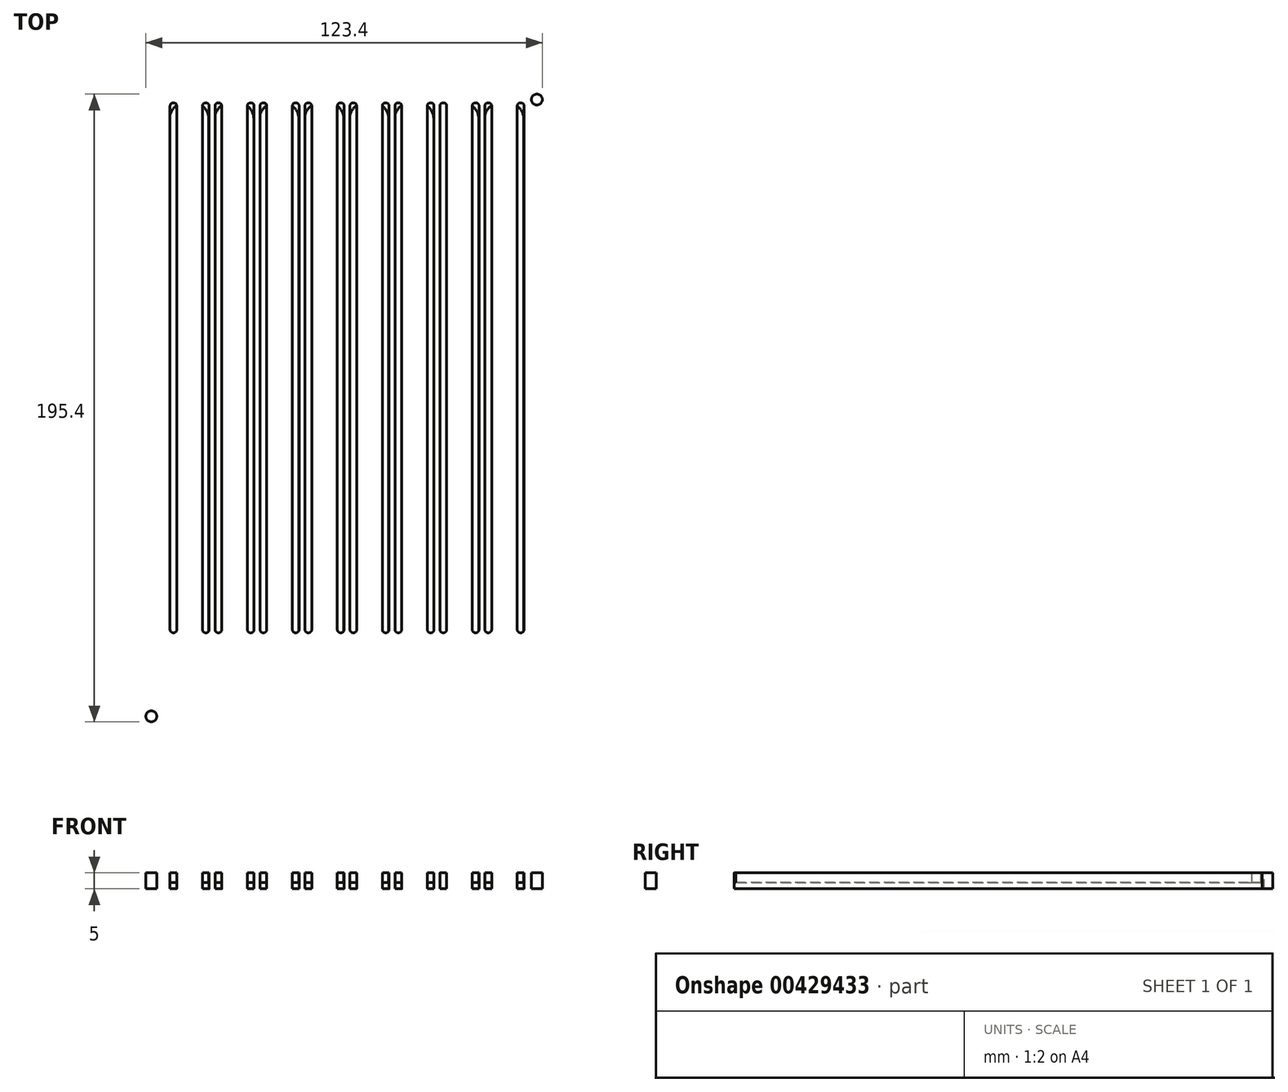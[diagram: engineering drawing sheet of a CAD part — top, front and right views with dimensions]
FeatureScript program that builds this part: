
annotation { "Feature Type Name" : "Feature", "Feature Type Description" : "" }
export const myFeature = defineFeature(function(context is Context, id is Id, definition is map)
    precondition{}
    {
        {
            var Q0;
            Q0=qCreatedBy(makeId("Top.planeOp"),FACE);
            var sketch = newSketch(context, id + "F0", { "sketchPlane" : qUnion([Q0])});
            skLineSegment(sketch, "E0.bottom", {"start": v(0, 200) * mm, "end": v(128, 200) * mm});
            skLineSegment(sketch, "E0.top", {"start": v(0, 0) * mm, "end": v(128, 0) * mm});
            skLineSegment(sketch, "E0.left", {"start": v(0, 200) * mm, "end": v(0, 0) * mm});
            skLineSegment(sketch, "E0.right", {"start": v(128, 200) * mm, "end": v(128, 0) * mm});
            skSolve(sketch);
        }
        {
            var Q0;
            Q0=makeQuery(id+"F0.imprint","IMPRINT",FACE,{"disambiguationData":[TD([[makeQuery(id+"F0.imprint","IMPRINT",EDGE,{"derivedFrom":sQuery(id+"F0.wireOp",EDGE,"E0.bottom")}),-1.0]])]});
            extrude(context, id + "F1", {"entities" : qUnion([Q0]), "depth" : 5 * mm});
        }
        {
            var Q0;
            Q0=makeQuery(id+"F1.opExtrude","CAP_FACE",FACE,{"disambiguationData":[OSD([sQuery(id+"F0.wireOp",EDGE,"E0.bottom"),sQuery(id+"F0.wireOp",EDGE,"E0.top"),sQuery(id+"F0.wireOp",EDGE,"E0.left"),sQuery(id+"F0.wireOp",EDGE,"E0.right")])],"isStart":false});
            var sketch = newSketch(context, id + "F2", { "sketchPlane" : qUnion([Q0])});
            skLineSegment(sketch, "E1.bottom", {"start": v(119, 195) * mm, "end": v(118.9, 195) * mm});
            skLineSegment(sketch, "E1.top", {"start": v(119, 30) * mm, "end": v(118.9, 30) * mm});
            skLineSegment(sketch, "E1.left", {"start": v(120, 194) * mm, "end": v(120, 31) * mm});
            skLineSegment(sketch, "E1.right", {"start": v(117.9, 194) * mm, "end": v(117.9, 31) * mm});
            skLineSegment(sketch, "E2.bottom", {"start": v(108.93, 195) * mm, "end": v(108.83, 195) * mm});
            skLineSegment(sketch, "E2.top", {"start": v(108.93, 30) * mm, "end": v(108.83, 30) * mm});
            skLineSegment(sketch, "E2.left", {"start": v(109.93, 194) * mm, "end": v(109.93, 31) * mm});
            skLineSegment(sketch, "E2.right", {"start": v(107.83, 194) * mm, "end": v(107.83, 31) * mm});
            skLineSegment(sketch, "E3", {"start": v(109.93, 30) * mm, "end": v(117.9, 30) * mm, "construction": true});
            skLineSegment(sketch, "E4", {"start": v(113.91, 30) * mm, "end": v(113.91, 0) * mm, "construction": true});
            skCircle(sketch, "E5", {"center": v(113.92, 6) * mm, "radius": 1.25 * mm});
            skPoint(sketch, "E6.visualSharp", {"position": v(117.9, 30) * mm});
            skArc(sketch, "E6.filletArc", {"start": v(117.9, 31) * mm, "mid": v(118.2, 30.3) * mm, "end": v(118.9, 30) * mm});
            skPoint(sketch, "E7.visualSharp", {"position": v(120, 30) * mm});
            skArc(sketch, "E7.filletArc", {"start": v(119, 30) * mm, "mid": v(119.7, 30.3) * mm, "end": v(120, 31) * mm});
            skPoint(sketch, "E8.visualSharp", {"position": v(109.93, 30) * mm});
            skArc(sketch, "E8.filletArc", {"start": v(108.93, 30) * mm, "mid": v(109.64, 30.3) * mm, "end": v(109.93, 31) * mm});
            skPoint(sketch, "E9.visualSharp", {"position": v(107.83, 30) * mm});
            skArc(sketch, "E9.filletArc", {"start": v(107.83, 31) * mm, "mid": v(108.12, 30.3) * mm, "end": v(108.83, 30) * mm});
            skPoint(sketch, "E10.visualSharp", {"position": v(120, 195) * mm});
            skArc(sketch, "E10.filletArc", {"start": v(120, 194) * mm, "mid": v(119.7, 194.7) * mm, "end": v(119, 195) * mm});
            skPoint(sketch, "E11.visualSharp", {"position": v(117.9, 195) * mm});
            skArc(sketch, "E11.filletArc", {"start": v(118.9, 195) * mm, "mid": v(118.2, 194.7) * mm, "end": v(117.9, 194) * mm});
            skPoint(sketch, "E12.visualSharp", {"position": v(109.93, 195) * mm});
            skArc(sketch, "E12.filletArc", {"start": v(109.93, 194) * mm, "mid": v(109.64, 194.7) * mm, "end": v(108.93, 195) * mm});
            skPoint(sketch, "E13.visualSharp", {"position": v(107.83, 195) * mm});
            skArc(sketch, "E13.filletArc", {"start": v(108.83, 195) * mm, "mid": v(108.12, 194.7) * mm, "end": v(107.83, 194) * mm});
            skCircle(sketch, "E14", {"center": v(124, 4) * mm, "radius": 1.7 * mm});
            skLineSegment(sketch, "E15", {"start": v(64, 0) * mm, "end": v(64, 22.65) * mm, "construction": true});
            skLineSegment(sketch, "E16", {"start": v(0, 100) * mm, "end": v(30.91, 100) * mm, "construction": true});
            skCircle(sketch, "E17.MirrorC", {"center": v(4, 4) * mm, "radius": 1.7 * mm});
            skCircle(sketch, "E18.MirrorC", {"center": v(4, 196) * mm, "radius": 1.7 * mm});
            skCircle(sketch, "E19.MirrorC", {"center": v(124, 196) * mm, "radius": 1.7 * mm});
            skCircle(sketch, "E20.1.0.0", {"center": v(99.92, 6) * mm, "radius": 1.25 * mm});
            skLineSegment(sketch, "E20.1.0.1", {"start": v(93.83, 194) * mm, "end": v(93.83, 31) * mm});
            skLineSegment(sketch, "E20.1.0.2", {"start": v(99.91, 30) * mm, "end": v(99.91, 0) * mm, "construction": true});
            skLineSegment(sketch, "E20.1.0.3", {"start": v(95.93, 30) * mm, "end": v(103.9, 30) * mm, "construction": true});
            skLineSegment(sketch, "E20.1.0.4", {"start": v(106, 194) * mm, "end": v(106, 31) * mm});
            skPoint(sketch, "E20.1.0.5", {"position": v(95.93, 30) * mm});
            skLineSegment(sketch, "E20.1.0.6", {"start": v(95.93, 194) * mm, "end": v(95.93, 31) * mm});
            skLineSegment(sketch, "E20.1.0.7", {"start": v(103.9, 194) * mm, "end": v(103.9, 31) * mm});
            skPoint(sketch, "E20.1.0.8", {"position": v(93.83, 30) * mm});
            skPoint(sketch, "E20.1.0.9", {"position": v(103.9, 30) * mm});
            skPoint(sketch, "E20.1.0.10", {"position": v(106, 30) * mm});
            skArc(sketch, "E20.1.0.11", {"start": v(94.93, 30) * mm, "mid": v(95.64, 30.3) * mm, "end": v(95.93, 31) * mm});
            skArc(sketch, "E20.1.0.12", {"start": v(93.83, 31) * mm, "mid": v(94.12, 30.3) * mm, "end": v(94.83, 30) * mm});
            skArc(sketch, "E20.1.0.13", {"start": v(105, 30) * mm, "mid": v(105.7, 30.3) * mm, "end": v(106, 31) * mm});
            skArc(sketch, "E20.1.0.14", {"start": v(103.9, 31) * mm, "mid": v(104.2, 30.3) * mm, "end": v(104.9, 30) * mm});
            skLineSegment(sketch, "E20.1.0.15", {"start": v(94.93, 30) * mm, "end": v(94.83, 30) * mm});
            skLineSegment(sketch, "E20.1.0.16", {"start": v(105, 30) * mm, "end": v(104.9, 30) * mm});
            skPoint(sketch, "E20.1.0.17", {"position": v(103.9, 195) * mm});
            skPoint(sketch, "E20.1.0.18", {"position": v(106, 195) * mm});
            skPoint(sketch, "E20.1.0.19", {"position": v(95.93, 195) * mm});
            skPoint(sketch, "E20.1.0.20", {"position": v(93.83, 195) * mm});
            skArc(sketch, "E20.1.0.21", {"start": v(94.83, 195) * mm, "mid": v(94.12, 194.7) * mm, "end": v(93.83, 194) * mm});
            skArc(sketch, "E20.1.0.22", {"start": v(95.93, 194) * mm, "mid": v(95.64, 194.7) * mm, "end": v(94.93, 195) * mm});
            skArc(sketch, "E20.1.0.23", {"start": v(106, 194) * mm, "mid": v(105.7, 194.7) * mm, "end": v(105, 195) * mm});
            skArc(sketch, "E20.1.0.24", {"start": v(104.9, 195) * mm, "mid": v(104.2, 194.7) * mm, "end": v(103.9, 194) * mm});
            skLineSegment(sketch, "E20.1.0.25", {"start": v(94.93, 195) * mm, "end": v(94.83, 195) * mm});
            skLineSegment(sketch, "E20.1.0.26", {"start": v(105, 195) * mm, "end": v(104.9, 195) * mm});
            skCircle(sketch, "E20.2.0.0", {"center": v(85.92, 6) * mm, "radius": 1.25 * mm});
            skLineSegment(sketch, "E20.2.0.1", {"start": v(79.83, 194) * mm, "end": v(79.83, 31) * mm});
            skLineSegment(sketch, "E20.2.0.2", {"start": v(85.91, 30) * mm, "end": v(85.91, 0) * mm, "construction": true});
            skLineSegment(sketch, "E20.2.0.3", {"start": v(81.93, 30) * mm, "end": v(89.9, 30) * mm, "construction": true});
            skLineSegment(sketch, "E20.2.0.4", {"start": v(92, 194) * mm, "end": v(92, 31) * mm});
            skPoint(sketch, "E20.2.0.5", {"position": v(81.93, 30) * mm});
            skLineSegment(sketch, "E20.2.0.6", {"start": v(81.93, 194) * mm, "end": v(81.93, 31) * mm});
            skLineSegment(sketch, "E20.2.0.7", {"start": v(89.9, 194) * mm, "end": v(89.9, 31) * mm});
            skPoint(sketch, "E20.2.0.8", {"position": v(79.83, 30) * mm});
            skPoint(sketch, "E20.2.0.9", {"position": v(89.9, 30) * mm});
            skPoint(sketch, "E20.2.0.10", {"position": v(92, 30) * mm});
            skArc(sketch, "E20.2.0.11", {"start": v(80.93, 30) * mm, "mid": v(81.64, 30.3) * mm, "end": v(81.93, 31) * mm});
            skArc(sketch, "E20.2.0.12", {"start": v(79.83, 31) * mm, "mid": v(80.12, 30.3) * mm, "end": v(80.83, 30) * mm});
            skArc(sketch, "E20.2.0.13", {"start": v(91, 30) * mm, "mid": v(91.7, 30.3) * mm, "end": v(92, 31) * mm});
            skArc(sketch, "E20.2.0.14", {"start": v(89.9, 31) * mm, "mid": v(90.2, 30.3) * mm, "end": v(90.9, 30) * mm});
            skLineSegment(sketch, "E20.2.0.15", {"start": v(80.93, 30) * mm, "end": v(80.83, 30) * mm});
            skLineSegment(sketch, "E20.2.0.16", {"start": v(91, 30) * mm, "end": v(90.9, 30) * mm});
            skPoint(sketch, "E20.2.0.17", {"position": v(89.9, 195) * mm});
            skPoint(sketch, "E20.2.0.18", {"position": v(92, 195) * mm});
            skPoint(sketch, "E20.2.0.19", {"position": v(81.93, 195) * mm});
            skPoint(sketch, "E20.2.0.20", {"position": v(79.83, 195) * mm});
            skArc(sketch, "E20.2.0.21", {"start": v(80.83, 195) * mm, "mid": v(80.12, 194.7) * mm, "end": v(79.83, 194) * mm});
            skArc(sketch, "E20.2.0.22", {"start": v(81.93, 194) * mm, "mid": v(81.64, 194.7) * mm, "end": v(80.93, 195) * mm});
            skArc(sketch, "E20.2.0.23", {"start": v(92, 194) * mm, "mid": v(91.7, 194.7) * mm, "end": v(91, 195) * mm});
            skArc(sketch, "E20.2.0.24", {"start": v(90.9, 195) * mm, "mid": v(90.2, 194.7) * mm, "end": v(89.9, 194) * mm});
            skLineSegment(sketch, "E20.2.0.25", {"start": v(80.93, 195) * mm, "end": v(80.83, 195) * mm});
            skLineSegment(sketch, "E20.2.0.26", {"start": v(91, 195) * mm, "end": v(90.9, 195) * mm});
            skCircle(sketch, "E20.3.0.0", {"center": v(71.92, 6) * mm, "radius": 1.25 * mm});
            skLineSegment(sketch, "E20.3.0.1", {"start": v(65.83, 194) * mm, "end": v(65.83, 31) * mm});
            skLineSegment(sketch, "E20.3.0.2", {"start": v(71.91, 30) * mm, "end": v(71.91, 0) * mm, "construction": true});
            skLineSegment(sketch, "E20.3.0.3", {"start": v(67.93, 30) * mm, "end": v(75.9, 30) * mm, "construction": true});
            skLineSegment(sketch, "E20.3.0.4", {"start": v(78, 194) * mm, "end": v(78, 31) * mm});
            skPoint(sketch, "E20.3.0.5", {"position": v(67.93, 30) * mm});
            skLineSegment(sketch, "E20.3.0.6", {"start": v(67.93, 194) * mm, "end": v(67.93, 31) * mm});
            skLineSegment(sketch, "E20.3.0.7", {"start": v(75.9, 194) * mm, "end": v(75.9, 31) * mm});
            skPoint(sketch, "E20.3.0.8", {"position": v(65.83, 30) * mm});
            skPoint(sketch, "E20.3.0.9", {"position": v(75.9, 30) * mm});
            skPoint(sketch, "E20.3.0.10", {"position": v(78, 30) * mm});
            skArc(sketch, "E20.3.0.11", {"start": v(66.93, 30) * mm, "mid": v(67.64, 30.3) * mm, "end": v(67.93, 31) * mm});
            skArc(sketch, "E20.3.0.12", {"start": v(65.83, 31) * mm, "mid": v(66.12, 30.3) * mm, "end": v(66.83, 30) * mm});
            skArc(sketch, "E20.3.0.13", {"start": v(77, 30) * mm, "mid": v(77.7, 30.3) * mm, "end": v(78, 31) * mm});
            skArc(sketch, "E20.3.0.14", {"start": v(75.9, 31) * mm, "mid": v(76.2, 30.3) * mm, "end": v(76.9, 30) * mm});
            skLineSegment(sketch, "E20.3.0.15", {"start": v(66.93, 30) * mm, "end": v(66.83, 30) * mm});
            skLineSegment(sketch, "E20.3.0.16", {"start": v(77, 30) * mm, "end": v(76.9, 30) * mm});
            skPoint(sketch, "E20.3.0.17", {"position": v(75.9, 195) * mm});
            skPoint(sketch, "E20.3.0.18", {"position": v(78, 195) * mm});
            skPoint(sketch, "E20.3.0.19", {"position": v(67.93, 195) * mm});
            skPoint(sketch, "E20.3.0.20", {"position": v(65.83, 195) * mm});
            skArc(sketch, "E20.3.0.21", {"start": v(66.83, 195) * mm, "mid": v(66.12, 194.7) * mm, "end": v(65.83, 194) * mm});
            skArc(sketch, "E20.3.0.22", {"start": v(67.93, 194) * mm, "mid": v(67.64, 194.7) * mm, "end": v(66.93, 195) * mm});
            skArc(sketch, "E20.3.0.23", {"start": v(78, 194) * mm, "mid": v(77.7, 194.7) * mm, "end": v(77, 195) * mm});
            skArc(sketch, "E20.3.0.24", {"start": v(76.9, 195) * mm, "mid": v(76.2, 194.7) * mm, "end": v(75.9, 194) * mm});
            skLineSegment(sketch, "E20.3.0.25", {"start": v(66.93, 195) * mm, "end": v(66.83, 195) * mm});
            skLineSegment(sketch, "E20.3.0.26", {"start": v(77, 195) * mm, "end": v(76.9, 195) * mm});
            skCircle(sketch, "E20.4.0.0", {"center": v(57.92, 6) * mm, "radius": 1.25 * mm});
            skLineSegment(sketch, "E20.4.0.1", {"start": v(51.83, 194) * mm, "end": v(51.83, 31) * mm});
            skLineSegment(sketch, "E20.4.0.2", {"start": v(57.91, 30) * mm, "end": v(57.91, 0) * mm, "construction": true});
            skLineSegment(sketch, "E20.4.0.3", {"start": v(53.93, 30) * mm, "end": v(61.9, 30) * mm, "construction": true});
            skLineSegment(sketch, "E20.4.0.4", {"start": v(64, 194) * mm, "end": v(64, 31) * mm});
            skPoint(sketch, "E20.4.0.5", {"position": v(53.93, 30) * mm});
            skLineSegment(sketch, "E20.4.0.6", {"start": v(53.93, 194) * mm, "end": v(53.93, 31) * mm});
            skLineSegment(sketch, "E20.4.0.7", {"start": v(61.9, 194) * mm, "end": v(61.9, 31) * mm});
            skPoint(sketch, "E20.4.0.8", {"position": v(51.83, 30) * mm});
            skPoint(sketch, "E20.4.0.9", {"position": v(61.9, 30) * mm});
            skPoint(sketch, "E20.4.0.10", {"position": v(64, 30) * mm});
            skArc(sketch, "E20.4.0.11", {"start": v(52.93, 30) * mm, "mid": v(53.64, 30.3) * mm, "end": v(53.93, 31) * mm});
            skArc(sketch, "E20.4.0.12", {"start": v(51.83, 31) * mm, "mid": v(52.12, 30.3) * mm, "end": v(52.83, 30) * mm});
            skArc(sketch, "E20.4.0.13", {"start": v(63, 30) * mm, "mid": v(63.7, 30.3) * mm, "end": v(64, 31) * mm});
            skArc(sketch, "E20.4.0.14", {"start": v(61.9, 31) * mm, "mid": v(62.2, 30.3) * mm, "end": v(62.9, 30) * mm});
            skLineSegment(sketch, "E20.4.0.15", {"start": v(52.93, 30) * mm, "end": v(52.83, 30) * mm});
            skLineSegment(sketch, "E20.4.0.16", {"start": v(63, 30) * mm, "end": v(62.9, 30) * mm});
            skPoint(sketch, "E20.4.0.17", {"position": v(61.9, 195) * mm});
            skPoint(sketch, "E20.4.0.18", {"position": v(64, 195) * mm});
            skPoint(sketch, "E20.4.0.19", {"position": v(53.93, 195) * mm});
            skPoint(sketch, "E20.4.0.20", {"position": v(51.83, 195) * mm});
            skArc(sketch, "E20.4.0.21", {"start": v(52.83, 195) * mm, "mid": v(52.12, 194.7) * mm, "end": v(51.83, 194) * mm});
            skArc(sketch, "E20.4.0.22", {"start": v(53.93, 194) * mm, "mid": v(53.64, 194.7) * mm, "end": v(52.93, 195) * mm});
            skArc(sketch, "E20.4.0.23", {"start": v(64, 194) * mm, "mid": v(63.7, 194.7) * mm, "end": v(63, 195) * mm});
            skArc(sketch, "E20.4.0.24", {"start": v(62.9, 195) * mm, "mid": v(62.2, 194.7) * mm, "end": v(61.9, 194) * mm});
            skLineSegment(sketch, "E20.4.0.25", {"start": v(52.93, 195) * mm, "end": v(52.83, 195) * mm});
            skLineSegment(sketch, "E20.4.0.26", {"start": v(63, 195) * mm, "end": v(62.9, 195) * mm});
            skCircle(sketch, "E20.5.0.0", {"center": v(43.92, 6) * mm, "radius": 1.25 * mm});
            skLineSegment(sketch, "E20.5.0.1", {"start": v(37.83, 194) * mm, "end": v(37.83, 31) * mm});
            skLineSegment(sketch, "E20.5.0.2", {"start": v(43.91, 30) * mm, "end": v(43.91, 0) * mm, "construction": true});
            skLineSegment(sketch, "E20.5.0.3", {"start": v(39.93, 30) * mm, "end": v(47.9, 30) * mm, "construction": true});
            skLineSegment(sketch, "E20.5.0.4", {"start": v(50, 194) * mm, "end": v(50, 31) * mm});
            skPoint(sketch, "E20.5.0.5", {"position": v(39.93, 30) * mm});
            skLineSegment(sketch, "E20.5.0.6", {"start": v(39.93, 194) * mm, "end": v(39.93, 31) * mm});
            skLineSegment(sketch, "E20.5.0.7", {"start": v(47.9, 194) * mm, "end": v(47.9, 31) * mm});
            skPoint(sketch, "E20.5.0.8", {"position": v(37.83, 30) * mm});
            skPoint(sketch, "E20.5.0.9", {"position": v(47.9, 30) * mm});
            skPoint(sketch, "E20.5.0.10", {"position": v(50, 30) * mm});
            skArc(sketch, "E20.5.0.11", {"start": v(38.93, 30) * mm, "mid": v(39.64, 30.3) * mm, "end": v(39.93, 31) * mm});
            skArc(sketch, "E20.5.0.12", {"start": v(37.83, 31) * mm, "mid": v(38.12, 30.3) * mm, "end": v(38.83, 30) * mm});
            skArc(sketch, "E20.5.0.13", {"start": v(49, 30) * mm, "mid": v(49.7, 30.3) * mm, "end": v(50, 31) * mm});
            skArc(sketch, "E20.5.0.14", {"start": v(47.9, 31) * mm, "mid": v(48.2, 30.3) * mm, "end": v(48.9, 30) * mm});
            skLineSegment(sketch, "E20.5.0.15", {"start": v(38.93, 30) * mm, "end": v(38.83, 30) * mm});
            skLineSegment(sketch, "E20.5.0.16", {"start": v(49, 30) * mm, "end": v(48.9, 30) * mm});
            skPoint(sketch, "E20.5.0.17", {"position": v(47.9, 195) * mm});
            skPoint(sketch, "E20.5.0.18", {"position": v(50, 195) * mm});
            skPoint(sketch, "E20.5.0.19", {"position": v(39.93, 195) * mm});
            skPoint(sketch, "E20.5.0.20", {"position": v(37.83, 195) * mm});
            skArc(sketch, "E20.5.0.21", {"start": v(38.83, 195) * mm, "mid": v(38.12, 194.7) * mm, "end": v(37.83, 194) * mm});
            skArc(sketch, "E20.5.0.22", {"start": v(39.93, 194) * mm, "mid": v(39.64, 194.7) * mm, "end": v(38.93, 195) * mm});
            skArc(sketch, "E20.5.0.23", {"start": v(50, 194) * mm, "mid": v(49.7, 194.7) * mm, "end": v(49, 195) * mm});
            skArc(sketch, "E20.5.0.24", {"start": v(48.9, 195) * mm, "mid": v(48.2, 194.7) * mm, "end": v(47.9, 194) * mm});
            skLineSegment(sketch, "E20.5.0.25", {"start": v(38.93, 195) * mm, "end": v(38.83, 195) * mm});
            skLineSegment(sketch, "E20.5.0.26", {"start": v(49, 195) * mm, "end": v(48.9, 195) * mm});
            skCircle(sketch, "E20.6.0.0", {"center": v(29.92, 6) * mm, "radius": 1.25 * mm});
            skLineSegment(sketch, "E20.6.0.1", {"start": v(23.83, 194) * mm, "end": v(23.83, 31) * mm});
            skLineSegment(sketch, "E20.6.0.2", {"start": v(29.91, 30) * mm, "end": v(29.91, 0) * mm, "construction": true});
            skLineSegment(sketch, "E20.6.0.3", {"start": v(25.93, 30) * mm, "end": v(33.9, 30) * mm, "construction": true});
            skLineSegment(sketch, "E20.6.0.4", {"start": v(36, 194) * mm, "end": v(36, 31) * mm});
            skPoint(sketch, "E20.6.0.5", {"position": v(25.93, 30) * mm});
            skLineSegment(sketch, "E20.6.0.6", {"start": v(25.93, 194) * mm, "end": v(25.93, 31) * mm});
            skLineSegment(sketch, "E20.6.0.7", {"start": v(33.9, 194) * mm, "end": v(33.9, 31) * mm});
            skPoint(sketch, "E20.6.0.8", {"position": v(23.83, 30) * mm});
            skPoint(sketch, "E20.6.0.9", {"position": v(33.9, 30) * mm});
            skPoint(sketch, "E20.6.0.10", {"position": v(36, 30) * mm});
            skArc(sketch, "E20.6.0.11", {"start": v(24.93, 30) * mm, "mid": v(25.64, 30.3) * mm, "end": v(25.93, 31) * mm});
            skArc(sketch, "E20.6.0.12", {"start": v(23.83, 31) * mm, "mid": v(24.12, 30.3) * mm, "end": v(24.83, 30) * mm});
            skArc(sketch, "E20.6.0.13", {"start": v(35, 30) * mm, "mid": v(35.7, 30.3) * mm, "end": v(36, 31) * mm});
            skArc(sketch, "E20.6.0.14", {"start": v(33.9, 31) * mm, "mid": v(34.2, 30.3) * mm, "end": v(34.9, 30) * mm});
            skLineSegment(sketch, "E20.6.0.15", {"start": v(24.93, 30) * mm, "end": v(24.83, 30) * mm});
            skLineSegment(sketch, "E20.6.0.16", {"start": v(35, 30) * mm, "end": v(34.9, 30) * mm});
            skPoint(sketch, "E20.6.0.17", {"position": v(33.9, 195) * mm});
            skPoint(sketch, "E20.6.0.18", {"position": v(36, 195) * mm});
            skPoint(sketch, "E20.6.0.19", {"position": v(25.93, 195) * mm});
            skPoint(sketch, "E20.6.0.20", {"position": v(23.83, 195) * mm});
            skArc(sketch, "E20.6.0.21", {"start": v(24.83, 195) * mm, "mid": v(24.12, 194.7) * mm, "end": v(23.83, 194) * mm});
            skArc(sketch, "E20.6.0.22", {"start": v(25.93, 194) * mm, "mid": v(25.64, 194.7) * mm, "end": v(24.93, 195) * mm});
            skArc(sketch, "E20.6.0.23", {"start": v(36, 194) * mm, "mid": v(35.7, 194.7) * mm, "end": v(35, 195) * mm});
            skArc(sketch, "E20.6.0.24", {"start": v(34.9, 195) * mm, "mid": v(34.2, 194.7) * mm, "end": v(33.9, 194) * mm});
            skLineSegment(sketch, "E20.6.0.25", {"start": v(24.93, 195) * mm, "end": v(24.83, 195) * mm});
            skLineSegment(sketch, "E20.6.0.26", {"start": v(35, 195) * mm, "end": v(34.9, 195) * mm});
            skCircle(sketch, "E20.7.0.0", {"center": v(15.92, 6) * mm, "radius": 1.25 * mm});
            skLineSegment(sketch, "E20.7.0.1", {"start": v(9.83, 194) * mm, "end": v(9.83, 31) * mm});
            skLineSegment(sketch, "E20.7.0.2", {"start": v(15.91, 30) * mm, "end": v(15.91, 0) * mm, "construction": true});
            skLineSegment(sketch, "E20.7.0.3", {"start": v(11.93, 30) * mm, "end": v(19.9, 30) * mm, "construction": true});
            skLineSegment(sketch, "E20.7.0.4", {"start": v(22, 194) * mm, "end": v(22, 31) * mm});
            skPoint(sketch, "E20.7.0.5", {"position": v(11.93, 30) * mm});
            skLineSegment(sketch, "E20.7.0.6", {"start": v(11.93, 194) * mm, "end": v(11.93, 31) * mm});
            skLineSegment(sketch, "E20.7.0.7", {"start": v(19.9, 194) * mm, "end": v(19.9, 31) * mm});
            skPoint(sketch, "E20.7.0.8", {"position": v(9.83, 30) * mm});
            skPoint(sketch, "E20.7.0.9", {"position": v(19.9, 30) * mm});
            skPoint(sketch, "E20.7.0.10", {"position": v(22, 30) * mm});
            skArc(sketch, "E20.7.0.11", {"start": v(10.93, 30) * mm, "mid": v(11.64, 30.3) * mm, "end": v(11.93, 31) * mm});
            skArc(sketch, "E20.7.0.12", {"start": v(9.83, 31) * mm, "mid": v(10.12, 30.3) * mm, "end": v(10.83, 30) * mm});
            skArc(sketch, "E20.7.0.13", {"start": v(21, 30) * mm, "mid": v(21.7, 30.3) * mm, "end": v(22, 31) * mm});
            skArc(sketch, "E20.7.0.14", {"start": v(19.9, 31) * mm, "mid": v(20.2, 30.3) * mm, "end": v(20.9, 30) * mm});
            skLineSegment(sketch, "E20.7.0.15", {"start": v(10.93, 30) * mm, "end": v(10.83, 30) * mm});
            skLineSegment(sketch, "E20.7.0.16", {"start": v(21, 30) * mm, "end": v(20.9, 30) * mm});
            skPoint(sketch, "E20.7.0.17", {"position": v(19.9, 195) * mm});
            skPoint(sketch, "E20.7.0.18", {"position": v(22, 195) * mm});
            skPoint(sketch, "E20.7.0.19", {"position": v(11.93, 195) * mm});
            skPoint(sketch, "E20.7.0.20", {"position": v(9.83, 195) * mm});
            skArc(sketch, "E20.7.0.21", {"start": v(10.83, 195) * mm, "mid": v(10.12, 194.7) * mm, "end": v(9.83, 194) * mm});
            skArc(sketch, "E20.7.0.22", {"start": v(11.93, 194) * mm, "mid": v(11.64, 194.7) * mm, "end": v(10.93, 195) * mm});
            skArc(sketch, "E20.7.0.23", {"start": v(22, 194) * mm, "mid": v(21.7, 194.7) * mm, "end": v(21, 195) * mm});
            skArc(sketch, "E20.7.0.24", {"start": v(20.9, 195) * mm, "mid": v(20.2, 194.7) * mm, "end": v(19.9, 194) * mm});
            skLineSegment(sketch, "E20.7.0.25", {"start": v(10.93, 195) * mm, "end": v(10.83, 195) * mm});
            skLineSegment(sketch, "E20.7.0.26", {"start": v(21, 195) * mm, "end": v(20.9, 195) * mm});
            skLineSegment(sketch, "E20.direction1", {"start": v(113.92, 6) * mm, "end": v(99.92, 6) * mm, "construction": true});
            skSolve(sketch);
        }
        {
            var Q0;
            Q0=makeQuery(id+"F2.imprint","IMPRINT",FACE,{"disambiguationData":[TD([[makeQuery(id+"F2.imprint","IMPRINT",EDGE,{"derivedFrom":sQuery(id+"F2.wireOp",EDGE,"E5")}),1.0]])]});
            var Q1;
            Q1=makeQuery(id+"F2.imprint","IMPRINT",FACE,{"disambiguationData":[TD([[makeQuery(id+"F2.imprint","IMPRINT",EDGE,{"derivedFrom":sQuery(id+"F2.wireOp",EDGE,"E18.MirrorC")}),1.0]])]});
            var Q2;
            Q2=makeQuery(id+"F2.imprint","IMPRINT",FACE,{"disambiguationData":[TD([[makeQuery(id+"F2.imprint","IMPRINT",EDGE,{"derivedFrom":sQuery(id+"F2.wireOp",EDGE,"E19.MirrorC")}),-1.0]])]});
            var Q3;
            Q3=makeQuery(id+"F2.imprint","IMPRINT",FACE,{"disambiguationData":[TD([[makeQuery(id+"F2.imprint","IMPRINT",EDGE,{"derivedFrom":sQuery(id+"F2.wireOp",EDGE,"E17.MirrorC")}),-1.0]])]});
            var Q4;
            Q4=makeQuery(id+"F2.imprint","IMPRINT",FACE,{"disambiguationData":[TD([[makeQuery(id+"F2.imprint","IMPRINT",EDGE,{"derivedFrom":sQuery(id+"F2.wireOp",EDGE,"E14")}),1.0]])]});
            var Q5;
            Q5=makeQuery(id+"F2.imprint","IMPRINT",FACE,{"disambiguationData":[TD([[makeQuery(id+"F2.imprint","IMPRINT",EDGE,{"derivedFrom":sQuery(id+"F2.wireOp",EDGE,"E20.5.0.0")}),1.0]])]});
            var Q6;
            Q6=makeQuery(id+"F2.imprint","IMPRINT",FACE,{"disambiguationData":[TD([[makeQuery(id+"F2.imprint","IMPRINT",EDGE,{"derivedFrom":sQuery(id+"F2.wireOp",EDGE,"E20.2.0.0")}),1.0]])]});
            var Q7;
            Q7=makeQuery(id+"F2.imprint","IMPRINT",FACE,{"disambiguationData":[TD([[makeQuery(id+"F2.imprint","IMPRINT",EDGE,{"derivedFrom":sQuery(id+"F2.wireOp",EDGE,"E20.3.0.0")}),1.0]])]});
            var Q8;
            Q8=makeQuery(id+"F2.imprint","IMPRINT",FACE,{"disambiguationData":[TD([[makeQuery(id+"F2.imprint","IMPRINT",EDGE,{"derivedFrom":sQuery(id+"F2.wireOp",EDGE,"E20.6.0.0")}),1.0]])]});
            var Q9;
            Q9=makeQuery(id+"F2.imprint","IMPRINT",FACE,{"disambiguationData":[TD([[makeQuery(id+"F2.imprint","IMPRINT",EDGE,{"derivedFrom":sQuery(id+"F2.wireOp",EDGE,"E20.7.0.0")}),1.0]])]});
            var Q10;
            Q10=makeQuery(id+"F2.imprint","IMPRINT",FACE,{"disambiguationData":[TD([[makeQuery(id+"F2.imprint","IMPRINT",EDGE,{"derivedFrom":sQuery(id+"F2.wireOp",EDGE,"E20.4.0.0")}),1.0]])]});
            var Q11;
            Q11=makeQuery(id+"F2.imprint","IMPRINT",FACE,{"disambiguationData":[TD([[makeQuery(id+"F2.imprint","IMPRINT",EDGE,{"derivedFrom":sQuery(id+"F2.wireOp",EDGE,"E20.1.0.0")}),1.0]])]});
            extrude(context, id + "F3", {"entities" : qUnion([Q0, Q1, Q2, Q3, Q4, Q5, Q6, Q7, Q8, Q9, Q10, Q11]), "operationType" : NewBodyOperationType.REMOVE, "oppositeDirection" : true, "depth" : 25 * mm});
        }
        {
            var Q0;
            Q0=makeQuery(id+"F1.opExtrude","CAP_FACE",FACE,{"disambiguationData":[OSD([sQuery(id+"F0.wireOp",EDGE,"E0.bottom"),sQuery(id+"F0.wireOp",EDGE,"E0.top"),sQuery(id+"F0.wireOp",EDGE,"E0.left"),sQuery(id+"F0.wireOp",EDGE,"E0.right")])],"isStart":false});
            var sketch = newSketch(context, id + "F4", { "sketchPlane" : qUnion([Q0])});
            skLineSegment(sketch, "E21.bottom", {"start": v(114.9, 195) * mm, "end": v(112.7, 195) * mm});
            skLineSegment(sketch, "E21.top", {"start": v(114.9, 25) * mm, "end": v(112.7, 25) * mm});
            skLineSegment(sketch, "E21.left", {"start": v(119.9, 190) * mm, "end": v(119.9, 30) * mm});
            skLineSegment(sketch, "E21.right", {"start": v(107.7, 190) * mm, "end": v(107.7, 30) * mm});
            skLineSegment(sketch, "E22.bottom", {"start": v(100.9, 195) * mm, "end": v(98.7, 195) * mm});
            skLineSegment(sketch, "E22.top", {"start": v(100.9, 25) * mm, "end": v(98.7, 25) * mm});
            skLineSegment(sketch, "E22.left", {"start": v(105.9, 190) * mm, "end": v(105.9, 30) * mm});
            skLineSegment(sketch, "E22.right", {"start": v(93.7, 190) * mm, "end": v(93.7, 30) * mm});
            skPoint(sketch, "E23.visualSharp", {"position": v(119.9, 195) * mm});
            skArc(sketch, "E23.filletArc", {"start": v(119.9, 190) * mm, "mid": v(118.44, 193.54) * mm, "end": v(114.9, 195) * mm});
            skPoint(sketch, "E24.visualSharp", {"position": v(107.7, 195) * mm});
            skArc(sketch, "E24.filletArc", {"start": v(112.7, 195) * mm, "mid": v(109.16, 193.54) * mm, "end": v(107.7, 190) * mm});
            skPoint(sketch, "E25.visualSharp", {"position": v(105.9, 195) * mm});
            skArc(sketch, "E25.filletArc", {"start": v(105.9, 190) * mm, "mid": v(104.44, 193.54) * mm, "end": v(100.9, 195) * mm});
            skPoint(sketch, "E26.visualSharp", {"position": v(93.7, 195) * mm});
            skArc(sketch, "E26.filletArc", {"start": v(98.7, 195) * mm, "mid": v(95.16, 193.54) * mm, "end": v(93.7, 190) * mm});
            skPoint(sketch, "E27.visualSharp", {"position": v(119.9, 25) * mm});
            skArc(sketch, "E27.filletArc", {"start": v(114.9, 25) * mm, "mid": v(118.44, 26.46) * mm, "end": v(119.9, 30) * mm});
            skPoint(sketch, "E28.visualSharp", {"position": v(107.7, 25) * mm});
            skArc(sketch, "E28.filletArc", {"start": v(107.7, 30) * mm, "mid": v(109.16, 26.46) * mm, "end": v(112.7, 25) * mm});
            skPoint(sketch, "E29.visualSharp", {"position": v(93.7, 25) * mm});
            skArc(sketch, "E29.filletArc", {"start": v(93.7, 30) * mm, "mid": v(95.16, 26.46) * mm, "end": v(98.7, 25) * mm});
            skPoint(sketch, "E30.visualSharp", {"position": v(105.9, 25) * mm});
            skArc(sketch, "E30.filletArc", {"start": v(100.9, 25) * mm, "mid": v(104.44, 26.46) * mm, "end": v(105.9, 30) * mm});
            skArc(sketch, "E31.1.0.0", {"start": v(84.7, 195) * mm, "mid": v(81.16, 193.54) * mm, "end": v(79.7, 190) * mm});
            skLineSegment(sketch, "E31.1.0.1", {"start": v(79.7, 190) * mm, "end": v(79.7, 30) * mm});
            skLineSegment(sketch, "E31.1.0.2", {"start": v(86.9, 195) * mm, "end": v(84.7, 195) * mm});
            skArc(sketch, "E31.1.0.3", {"start": v(91.9, 190) * mm, "mid": v(90.44, 193.54) * mm, "end": v(86.9, 195) * mm});
            skLineSegment(sketch, "E31.1.0.4", {"start": v(91.9, 190) * mm, "end": v(91.9, 30) * mm});
            skArc(sketch, "E31.1.0.5", {"start": v(86.9, 25) * mm, "mid": v(90.44, 26.46) * mm, "end": v(91.9, 30) * mm});
            skLineSegment(sketch, "E31.1.0.6", {"start": v(86.9, 25) * mm, "end": v(84.7, 25) * mm});
            skArc(sketch, "E31.1.0.7", {"start": v(79.7, 30) * mm, "mid": v(81.16, 26.46) * mm, "end": v(84.7, 25) * mm});
            skArc(sketch, "E31.2.0.0", {"start": v(70.7, 195) * mm, "mid": v(67.16, 193.54) * mm, "end": v(65.7, 190) * mm});
            skLineSegment(sketch, "E31.2.0.1", {"start": v(65.7, 190) * mm, "end": v(65.7, 30) * mm});
            skLineSegment(sketch, "E31.2.0.2", {"start": v(72.9, 195) * mm, "end": v(70.7, 195) * mm});
            skArc(sketch, "E31.2.0.3", {"start": v(77.9, 190) * mm, "mid": v(76.44, 193.54) * mm, "end": v(72.9, 195) * mm});
            skLineSegment(sketch, "E31.2.0.4", {"start": v(77.9, 190) * mm, "end": v(77.9, 30) * mm});
            skArc(sketch, "E31.2.0.5", {"start": v(72.9, 25) * mm, "mid": v(76.44, 26.46) * mm, "end": v(77.9, 30) * mm});
            skLineSegment(sketch, "E31.2.0.6", {"start": v(72.9, 25) * mm, "end": v(70.7, 25) * mm});
            skArc(sketch, "E31.2.0.7", {"start": v(65.7, 30) * mm, "mid": v(67.16, 26.46) * mm, "end": v(70.7, 25) * mm});
            skArc(sketch, "E31.3.0.0", {"start": v(56.7, 195) * mm, "mid": v(53.16, 193.54) * mm, "end": v(51.7, 190) * mm});
            skLineSegment(sketch, "E31.3.0.1", {"start": v(51.7, 190) * mm, "end": v(51.7, 30) * mm});
            skLineSegment(sketch, "E31.3.0.2", {"start": v(58.9, 195) * mm, "end": v(56.7, 195) * mm});
            skArc(sketch, "E31.3.0.3", {"start": v(63.9, 190) * mm, "mid": v(62.44, 193.54) * mm, "end": v(58.9, 195) * mm});
            skLineSegment(sketch, "E31.3.0.4", {"start": v(63.9, 190) * mm, "end": v(63.9, 30) * mm});
            skArc(sketch, "E31.3.0.5", {"start": v(58.9, 25) * mm, "mid": v(62.44, 26.46) * mm, "end": v(63.9, 30) * mm});
            skLineSegment(sketch, "E31.3.0.6", {"start": v(58.9, 25) * mm, "end": v(56.7, 25) * mm});
            skArc(sketch, "E31.3.0.7", {"start": v(51.7, 30) * mm, "mid": v(53.16, 26.46) * mm, "end": v(56.7, 25) * mm});
            skArc(sketch, "E31.4.0.0", {"start": v(42.7, 195) * mm, "mid": v(39.16, 193.54) * mm, "end": v(37.7, 190) * mm});
            skLineSegment(sketch, "E31.4.0.1", {"start": v(37.7, 190) * mm, "end": v(37.7, 30) * mm});
            skLineSegment(sketch, "E31.4.0.2", {"start": v(44.9, 195) * mm, "end": v(42.7, 195) * mm});
            skArc(sketch, "E31.4.0.3", {"start": v(49.9, 190) * mm, "mid": v(48.44, 193.54) * mm, "end": v(44.9, 195) * mm});
            skLineSegment(sketch, "E31.4.0.4", {"start": v(49.9, 190) * mm, "end": v(49.9, 30) * mm});
            skArc(sketch, "E31.4.0.5", {"start": v(44.9, 25) * mm, "mid": v(48.44, 26.46) * mm, "end": v(49.9, 30) * mm});
            skLineSegment(sketch, "E31.4.0.6", {"start": v(44.9, 25) * mm, "end": v(42.7, 25) * mm});
            skArc(sketch, "E31.4.0.7", {"start": v(37.7, 30) * mm, "mid": v(39.16, 26.46) * mm, "end": v(42.7, 25) * mm});
            skArc(sketch, "E31.5.0.0", {"start": v(28.7, 195) * mm, "mid": v(25.16, 193.54) * mm, "end": v(23.7, 190) * mm});
            skLineSegment(sketch, "E31.5.0.1", {"start": v(23.7, 190) * mm, "end": v(23.7, 30) * mm});
            skLineSegment(sketch, "E31.5.0.2", {"start": v(30.9, 195) * mm, "end": v(28.7, 195) * mm});
            skArc(sketch, "E31.5.0.3", {"start": v(35.9, 190) * mm, "mid": v(34.44, 193.54) * mm, "end": v(30.9, 195) * mm});
            skLineSegment(sketch, "E31.5.0.4", {"start": v(35.9, 190) * mm, "end": v(35.9, 30) * mm});
            skArc(sketch, "E31.5.0.5", {"start": v(30.9, 25) * mm, "mid": v(34.44, 26.46) * mm, "end": v(35.9, 30) * mm});
            skLineSegment(sketch, "E31.5.0.6", {"start": v(30.9, 25) * mm, "end": v(28.7, 25) * mm});
            skArc(sketch, "E31.5.0.7", {"start": v(23.7, 30) * mm, "mid": v(25.16, 26.46) * mm, "end": v(28.7, 25) * mm});
            skArc(sketch, "E31.6.0.0", {"start": v(14.7, 195) * mm, "mid": v(11.16, 193.54) * mm, "end": v(9.7, 190) * mm});
            skLineSegment(sketch, "E31.6.0.1", {"start": v(9.7, 190) * mm, "end": v(9.7, 30) * mm});
            skLineSegment(sketch, "E31.6.0.2", {"start": v(16.9, 195) * mm, "end": v(14.7, 195) * mm});
            skArc(sketch, "E31.6.0.3", {"start": v(21.9, 190) * mm, "mid": v(20.44, 193.54) * mm, "end": v(16.9, 195) * mm});
            skLineSegment(sketch, "E31.6.0.4", {"start": v(21.9, 190) * mm, "end": v(21.9, 30) * mm});
            skArc(sketch, "E31.6.0.5", {"start": v(16.9, 25) * mm, "mid": v(20.44, 26.46) * mm, "end": v(21.9, 30) * mm});
            skLineSegment(sketch, "E31.6.0.6", {"start": v(16.9, 25) * mm, "end": v(14.7, 25) * mm});
            skArc(sketch, "E31.6.0.7", {"start": v(9.7, 30) * mm, "mid": v(11.16, 26.46) * mm, "end": v(14.7, 25) * mm});
            skLineSegment(sketch, "E31.direction1", {"start": v(93.7, 190) * mm, "end": v(79.7, 190) * mm, "construction": true});
            skSolve(sketch);
        }
        {
            var Q0;
            {var subQ9=sQuery(id+"F4.wireOp",EDGE,"E21.bottom");Q0=makeQuery(id+"F4.imprint","IMPRINT",FACE,{"disambiguationData":[TD([[makeQuery(id+"F4.imprint","IMPRINT",EDGE,{"derivedFrom":subQ9}),1.0]])]});}
            var Q1;
            {var subQ5=sQuery(id+"F4.wireOp",EDGE,"E22.bottom");Q1=makeQuery(id+"F4.imprint","IMPRINT",FACE,{"disambiguationData":[TD([[makeQuery(id+"F4.imprint","IMPRINT",EDGE,{"derivedFrom":subQ5}),1.0]])]});}
            var Q2;
            Q2=makeQuery(id+"F4.imprint","IMPRINT",FACE,{"disambiguationData":[TD([[makeQuery(id+"F4.imprint","IMPRINT",EDGE,{"derivedFrom":sQuery(id+"F4.wireOp",EDGE,"E31.1.0.0")}),1.0]])]});
            var Q3;
            Q3=makeQuery(id+"F4.imprint","IMPRINT",FACE,{"disambiguationData":[TD([[makeQuery(id+"F4.imprint","IMPRINT",EDGE,{"derivedFrom":sQuery(id+"F4.wireOp",EDGE,"E31.2.0.0")}),1.0]])]});
            var Q4;
            Q4=makeQuery(id+"F4.imprint","IMPRINT",FACE,{"disambiguationData":[TD([[makeQuery(id+"F4.imprint","IMPRINT",EDGE,{"derivedFrom":sQuery(id+"F4.wireOp",EDGE,"E31.3.0.0")}),1.0]])]});
            var Q5;
            Q5=makeQuery(id+"F4.imprint","IMPRINT",FACE,{"disambiguationData":[TD([[makeQuery(id+"F4.imprint","IMPRINT",EDGE,{"derivedFrom":sQuery(id+"F4.wireOp",EDGE,"E31.4.0.0")}),1.0]])]});
            var Q6;
            Q6=makeQuery(id+"F4.imprint","IMPRINT",FACE,{"disambiguationData":[TD([[makeQuery(id+"F4.imprint","IMPRINT",EDGE,{"derivedFrom":sQuery(id+"F4.wireOp",EDGE,"E31.5.0.0")}),1.0]])]});
            var Q7;
            Q7=makeQuery(id+"F4.imprint","IMPRINT",FACE,{"disambiguationData":[TD([[makeQuery(id+"F4.imprint","IMPRINT",EDGE,{"derivedFrom":sQuery(id+"F4.wireOp",EDGE,"E31.6.0.0")}),1.0]])]});
            extrude(context, id + "F5", {"entities" : qUnion([Q0, Q1, Q2, Q3, Q4, Q5, Q6, Q7]), "operationType" : NewBodyOperationType.REMOVE, "oppositeDirection" : true, "depth" : 3 * mm});
        }
    });
